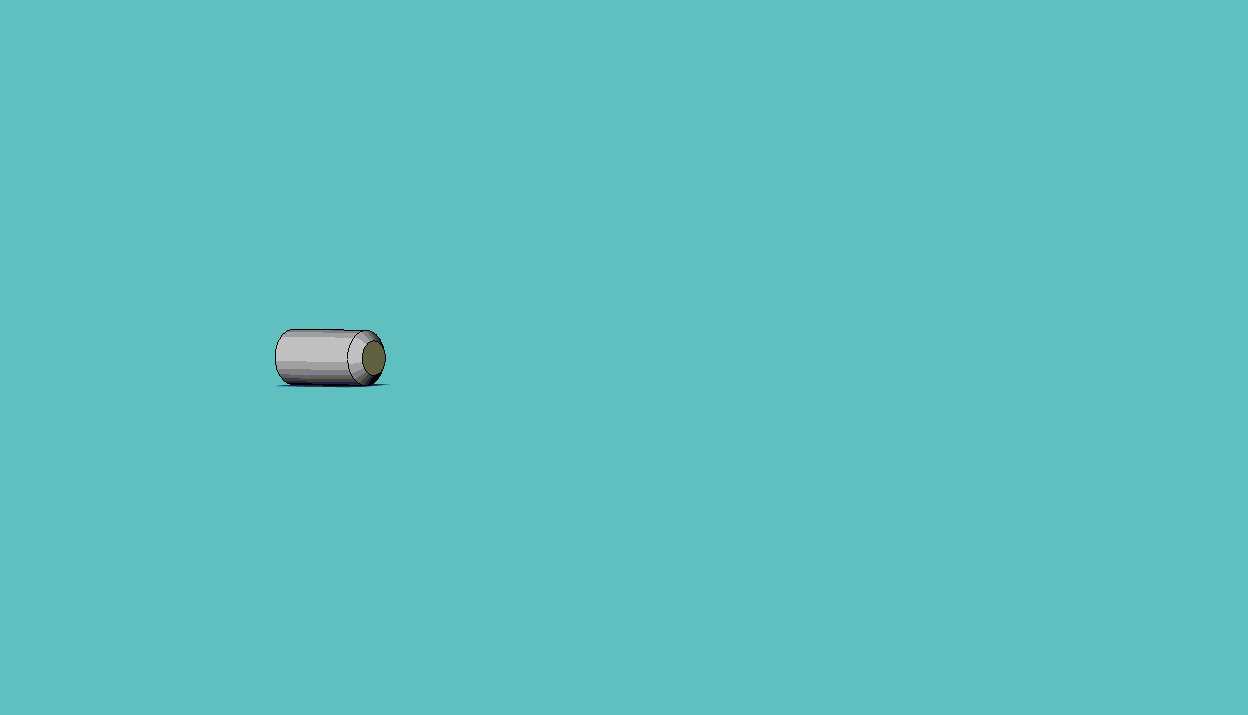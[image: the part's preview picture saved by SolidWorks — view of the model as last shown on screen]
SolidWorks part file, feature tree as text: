
SOLIDWORKS PART (.sldprt)
format: sldprt  version: not decoded by parser v0  size: 174,592 bytes
history: native  units: mm
features: plane x3, sketch x3, material x1, revolve x1, thread x1, cut_extrude x1, cut_revolve x1, pattern_linear x1 (+8 scaffold rows collapsed)
feature tree (20):
  scaffold x8  (default folders/planes/origin — collapsed)
  material  "Matériau <non spécifié>"
  plane  "Plane1"
  plane  "Plane2"
  plane  "Plane3"
  sketch  "BodySke"  dims[c1.D1=~35.921024mm c2.D1=270.0deg c3.D1=~35.921024mm c3.Cone_ang=90.0deg c3.Length=50.8mm c3.Diameter=4.0mm c3.D4=~4.490128mm c3.Drive_ch_ang=60.0deg c3.Minor_dia=3.22mm c4.D1=~8.980256mm c4.Cup_nose_ang=45.0deg c5.D1=~7.099516mm c5.Cup_ang=118.0deg c5.Cup_dia=2.5mm c5.Length=8.0mm c5.Advance=0.7mm c5.Head_ht=~1.88976mm c5.BodyLength=~43.94454mm]
  revolve  "BaseBody"  [1 undecoded]
  thread  "ThreadCosmetic"  Diameter=3.22mm Thread_minor=3.22mm  [1 undecoded]
  sketch  "Sketch2"  dims[Hex_size=2.0mm D2=1.0mm D3=1.0mm]
  cut_extrude  "Hex"  Depth=2.5mm Key_eng=2.5mm
  sketch  "ThdSchSke"  dims[c1.Thread_minor=~1.03886mm c1.Diameter=~1.413535mm c1.Start=~0.988134mm c1.D4=~4.446753mm c1.Vee=60.0deg c2.Thread_minor=~1.03886mm c2.Start=~2.540025mm c2.D1=~0.108159mm c2.D2=~0.108159mm c3.D1=~0.216319mm c3.SideAngle=55.0deg c3.D2=~0.216319mm c3.VeeAngle=70.0deg c3.Thread_minor=3.22mm c3.Overcut=5.0mm c3.Diameter=4.0mm c3.D6=~8.326268mm c4.D1=~8.326268mm c5.D1=90.0deg c5.Start=63.5mm c6.Start=20.5486mm c7.Start=~1.88976mm]
  cut_revolve  "ThreadSchematic"  Angle=360deg
  pattern_linear  "ThdSchPat"  Count1=12 Count2=1 Spacing1=0.638621mm Spacing2=50mm Num_threads=12 Advance=0.638621mm ConfigurationName=0mm CopiedFlag=1 PartNumberID=0mm
decode coverage: 7 of 8 modeling features carry decoded parameters
note: ~ marks probable driven/reference dimensions
note: 2 parameter values undecoded
note: suppression state not decoded; provenance and decode notes live in map.json
